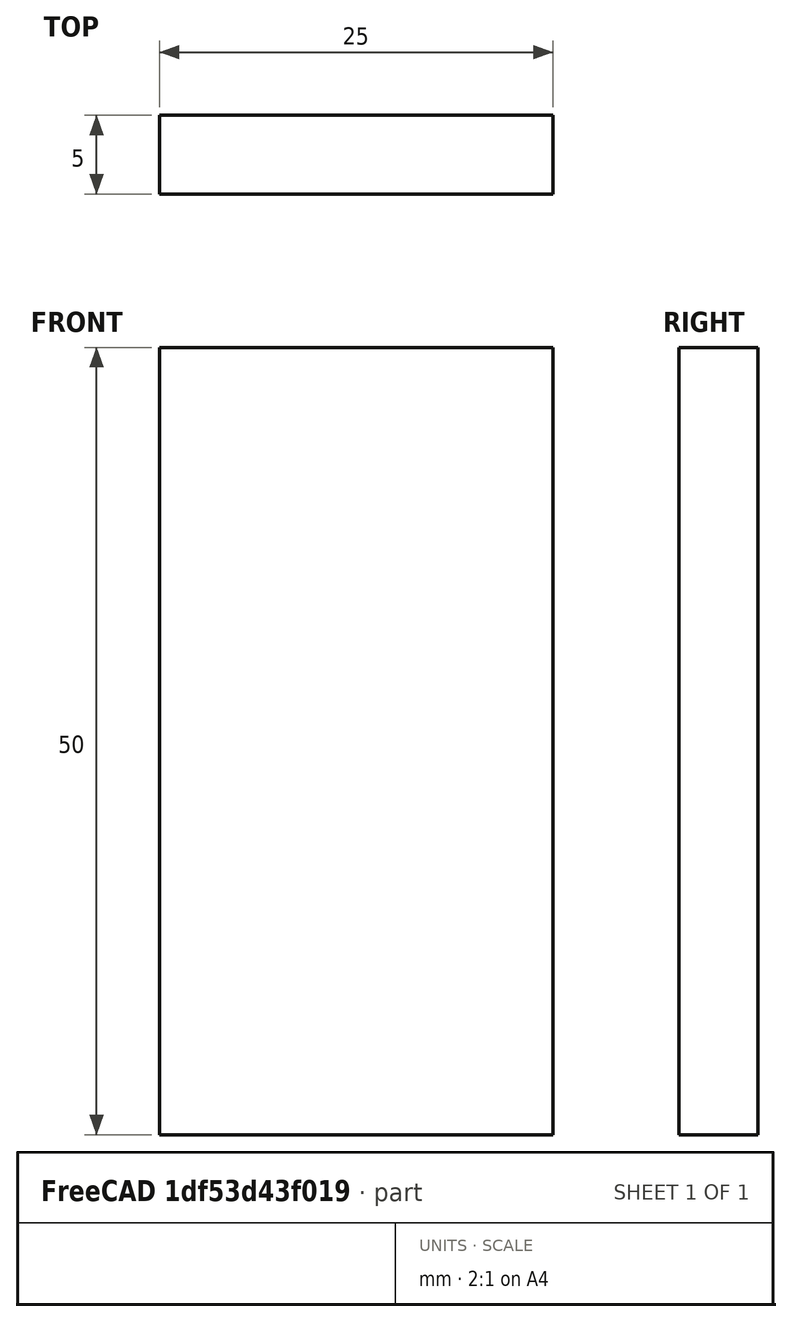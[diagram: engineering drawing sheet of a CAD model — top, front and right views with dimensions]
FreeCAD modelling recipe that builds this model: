
FCSTD DOCUMENT  (FreeCAD 0.15R4671 (Git))
Label: Flat Bar 25x5 EN10058 S235JR
License: All rights reserved
LicenseURL: http://en.wikipedia.org/wiki/All_rights_reserved
objects: Sketcher::SketchObject×1, Part::Extrusion×1
note: 2 computed .brp shape members not serialized (recipe doc carries the construction recipe); baked Part::Feature solids carry a one-line shape summary decoded from their .brp

FEATURE [Sketcher::SketchObject] Sketch
  sketch-geometry (4):
    g0: LineSegment StartX=-12.5 StartY=-2.5 StartZ=0 EndX=12.5 EndY=-2.5 EndZ=0
    g1: LineSegment StartX=12.5 StartY=-2.5 StartZ=0 EndX=12.5 EndY=2.5 EndZ=0
    g2: LineSegment StartX=12.5 StartY=2.5 StartZ=0 EndX=-12.5 EndY=2.5 EndZ=0
    g3: LineSegment StartX=-12.5 StartY=2.5 StartZ=0 EndX=-12.5 EndY=-2.5 EndZ=0
  constraints (12):
    c: Coincident(g0,g1)
    c: Coincident(g1,g2)
    c: Coincident(g2,g3)
    c: Coincident(g3,g0)
    c: Horizontal(g0)
    c: Horizontal(g2)
    c: Vertical(g1)
    c: Vertical(g3)
    c: Symmetric(g1,g2,g-2)
    c: Symmetric(g0,g1,g-1)
    c: DistanceY(g1) = 5
    c: DistanceX(g0) = 25
FEATURE [Part::Extrusion] Extrude  label="Flat Bar 25x5 EN10058 S235JR"
  Base = -> Sketch
  Dir = (0,0,50)
  Solid = true
